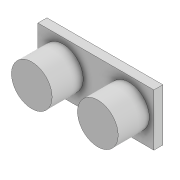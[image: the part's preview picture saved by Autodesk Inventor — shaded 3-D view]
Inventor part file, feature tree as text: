
AUTODESK INVENTOR PART (.ipt)
format: ipt  version: 2020 (Build 240168000, 168)  size: 114,688 bytes
history: native  units: mm
features: extrude x3, sketch x3
ambient origin geometry x8: Origin, YZ Plane, XZ Plane, XY Plane, X Axis, Y Axis, Z Axis, Center Point
bodies: Volumenkörper1 (feature_tree)
feature tree (6):
  extrude  "Extrusion1"  Depth=45.1mm
  extrude  "Extrusion2"  Depth=3.5mm
  extrude  "Extrusion3"  Depth=17.55mm
  sketch  "Skizze1"  dims[d0=20.3mm d1=45.1mm]
  sketch  "Skizze2"  dims[d2=3.5mm d3=0.0mm d4=15.8mm]
  sketch  "Skizze3"  dims[d5=15.8mm d6=25.7mm d8=9.7mm d9=10.2mm d10=10.2mm d11=12.1mm d12=0.0mm d13=2.7mm d14=2.3mm d15=4.0mm d16=0.0mm d17=10.0mm d18=17.55mm]
